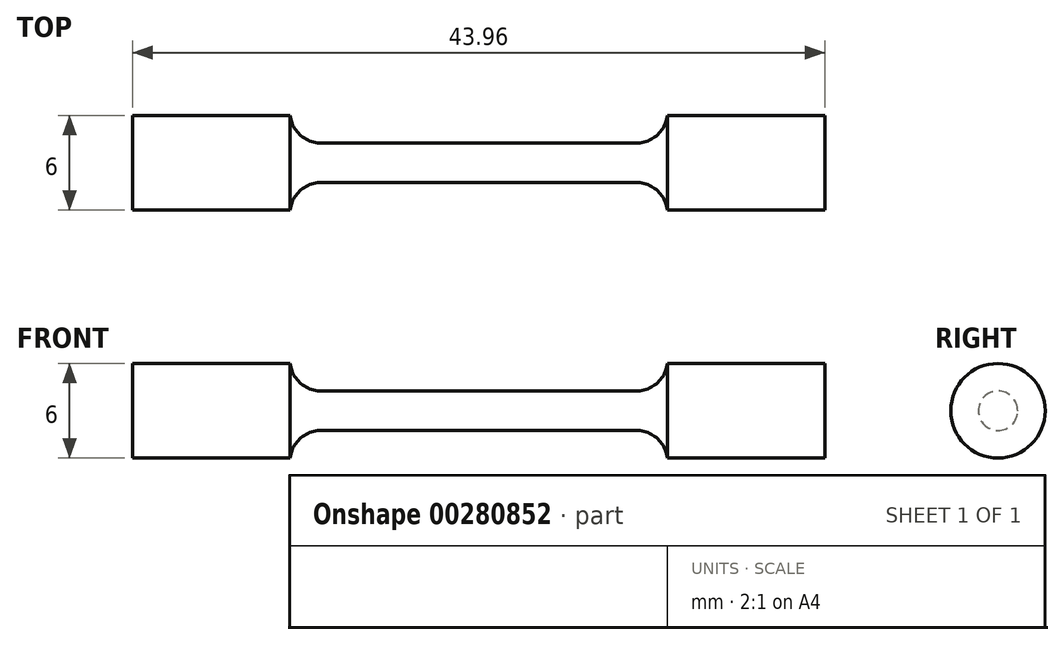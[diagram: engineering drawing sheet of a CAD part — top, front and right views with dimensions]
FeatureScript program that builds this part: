
annotation { "Feature Type Name" : "Feature", "Feature Type Description" : "" }
export const myFeature = defineFeature(function(context is Context, id is Id, definition is map)
    precondition{}
    {
        {
            var Q0;
            Q0=qCreatedBy(makeId("Front.planeOp"),FACE);
            var sketch = newSketch(context, id + "F0", { "sketchPlane" : qUnion([Q0])});
            skLineSegment(sketch, "E0", {"start": v(0, 0) * mm, "end": v(0, 1.25) * mm});
            skLineSegment(sketch, "E1", {"start": v(0, 1.25) * mm, "end": v(10, 1.25) * mm});
            skArc(sketch, "E2", {"start": v(10, 1.25) * mm, "mid": v(11.32, 1.75) * mm, "end": v(11.98, 3) * mm});
            skLineSegment(sketch, "E3", {"start": v(11.98, 3) * mm, "end": v(21.98, 3) * mm});
            skLineSegment(sketch, "E4", {"start": v(21.98, 3) * mm, "end": v(21.98, 0) * mm});
            skArc(sketch, "E5.MirrorCS", {"start": v(-10, 1.25) * mm, "mid": v(-11.32, 1.75) * mm, "end": v(-11.98, 3) * mm});
            skLineSegment(sketch, "E6.MirrorCS", {"start": v(-11.98, 3) * mm, "end": v(-21.98, 3) * mm});
            skLineSegment(sketch, "E7.MirrorCS", {"start": v(0, 1.25) * mm, "end": v(-10, 1.25) * mm});
            skLineSegment(sketch, "E8.MirrorCS", {"start": v(-21.98, 3) * mm, "end": v(-21.98, 0) * mm});
            skLineSegment(sketch, "E9", {"start": v(-21.98, 0) * mm, "end": v(21.98, 0) * mm});
            skSolve(sketch);
        }
        {
            var Q0;
            Q0=qSketchRegion(id+"F0",true);
            var Q1;
            Q1=sQuery(id+"F0.wireOp",EDGE,"E9");
            revolve(context, id + "F1", {"entities" : qUnion([Q0]), "axis" : qUnion([Q1]), "revolveType" : RevolveType.FULL});
        }
    });
